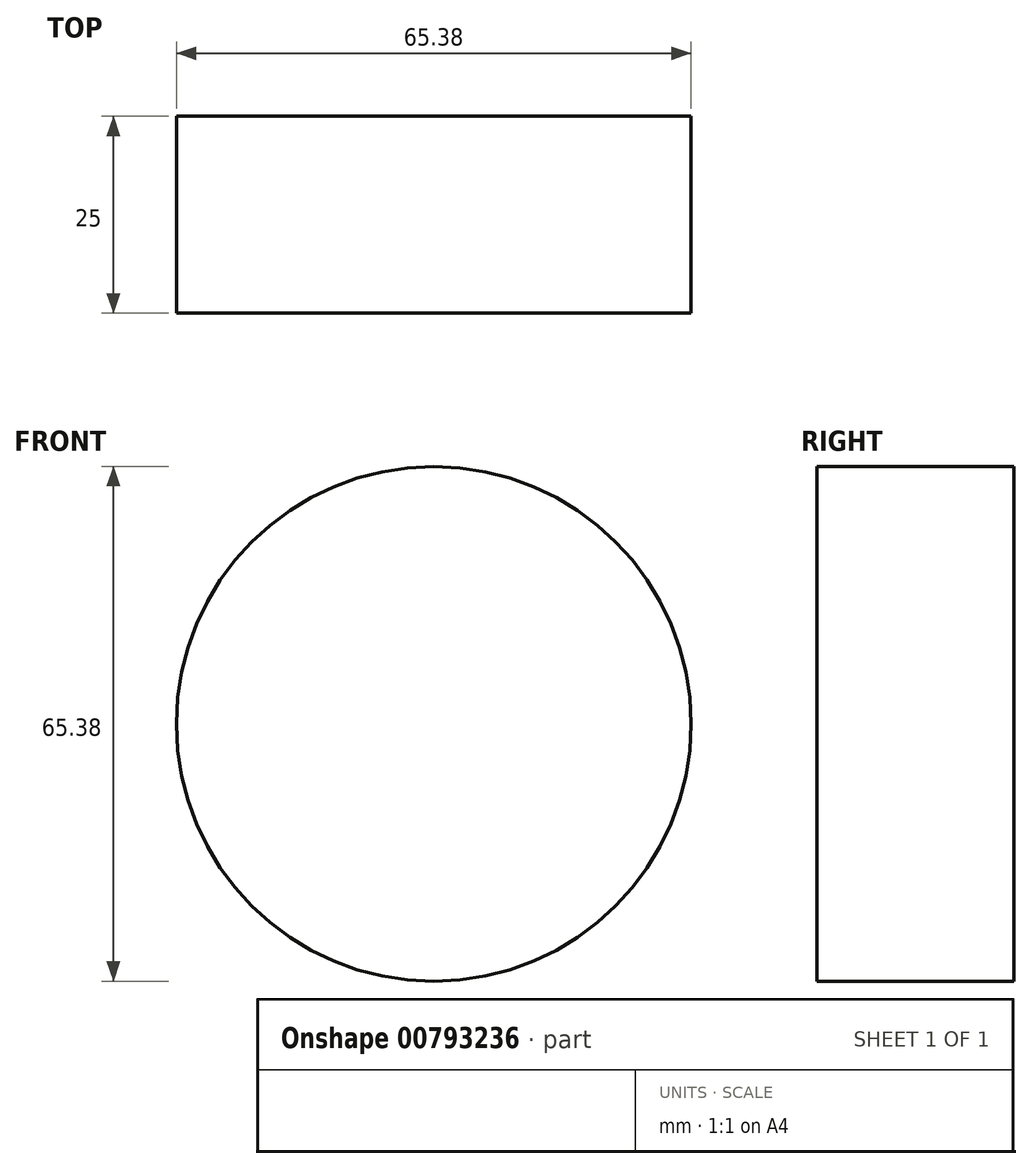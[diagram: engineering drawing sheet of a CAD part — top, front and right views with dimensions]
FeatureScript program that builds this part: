
annotation { "Feature Type Name" : "Feature", "Feature Type Description" : "" }
export const myFeature = defineFeature(function(context is Context, id is Id, definition is map)
    precondition{}
    {
        {
            var Q0;
            Q0=qCreatedBy(makeId("Front.planeOp"),FACE);
            var sketch = newSketch(context, id + "F0", { "sketchPlane" : qUnion([Q0])});
            skCircle(sketch, "E0", {"center": v(-93.47, 15.05) * mm, "radius": 32.7 * mm});
            skSolve(sketch);
        }
        {
            var Q0;
            Q0 = qSketchRegion(id + "F0", true);
            extrude(context, id + "F1", {"entities" : qUnion([Q0]), "depth" : 25 * mm, "offsetDistance" : 25 * mm});
        }
    });
